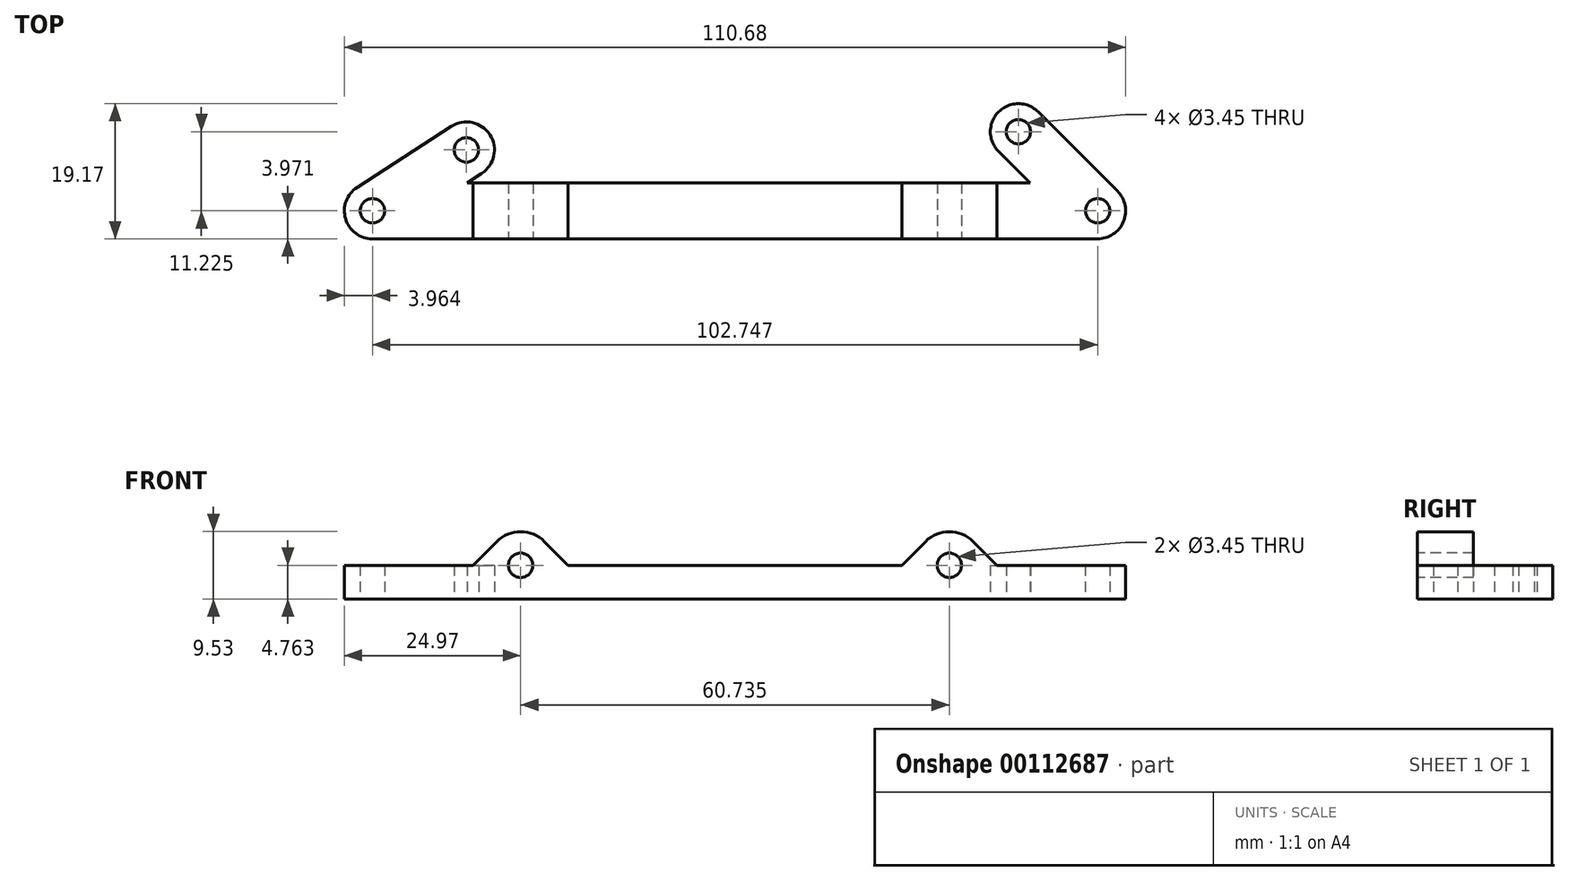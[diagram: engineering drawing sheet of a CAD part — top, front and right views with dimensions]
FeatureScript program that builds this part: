
annotation { "Feature Type Name" : "Feature", "Feature Type Description" : "" }
export const myFeature = defineFeature(function(context is Context, id is Id, definition is map)
    precondition{}
    {
        {
            var Q0;
            Q0=qCreatedBy(makeId("Top.planeOp"),FACE);
            var sketch = newSketch(context, id + "F0", { "sketchPlane" : qUnion([Q0])});
            skLineSegment(sketch, "E0", {"start": v(0, 0) * mm, "end": v(-79.74, 0) * mm});
            skLineSegment(sketch, "E1", {"start": v(0, 0) * mm, "end": v(-4.45, 4.45) * mm});
            skLineSegment(sketch, "E2", {"start": v(-79.74, 0) * mm, "end": v(-77.68, 1.33) * mm});
            skLineSegment(sketch, "E3", {"start": v(-39.87, 0) * mm, "end": v(-39.87, -7.94) * mm, "construction": true});
            skLineSegment(sketch, "E4", {"start": v(-93.17, -7.94) * mm, "end": v(9.58, -7.94) * mm});
            skLineSegment(sketch, "E5", {"start": v(-77.68, 1.33) * mm, "end": v(-82, 8) * mm, "construction": true});
            skLineSegment(sketch, "E6", {"start": v(-4.45, 4.45) * mm, "end": v(1.16, 10.06) * mm, "construction": true});
            skArc(sketch, "E7", {"start": v(-95.32, -0.64) * mm, "mid": v(-96.97, -5.1) * mm, "end": v(-93.17, -7.94) * mm});
            skArc(sketch, "E8", {"start": v(9.58, -7.94) * mm, "mid": v(13.25, -5.49) * mm, "end": v(12.39, -1.16) * mm});
            skArc(sketch, "E9", {"start": v(-77.68, 1.33) * mm, "mid": v(-76.51, 6.82) * mm, "end": v(-82, 8) * mm});
            skArc(sketch, "E10", {"start": v(1.16, 10.06) * mm, "mid": v(-4.45, 10.06) * mm, "end": v(-4.45, 4.45) * mm});
            skLineSegment(sketch, "E11", {"start": v(-93.17, -3.97) * mm, "end": v(-79.84, 4.66) * mm, "construction": true});
            skLineSegment(sketch, "E12", {"start": v(-95.32, -0.64) * mm, "end": v(-82, 8) * mm});
            skLineSegment(sketch, "E13", {"start": v(1.16, 10.06) * mm, "end": v(12.39, -1.16) * mm});
            skLineSegment(sketch, "E14", {"start": v(-1.64, 7.26) * mm, "end": v(9.58, -3.97) * mm, "construction": true});
            skCircle(sketch, "E15", {"center": v(-79.84, 4.66) * mm, "radius": 1.73 * mm});
            skCircle(sketch, "E16", {"center": v(-93.17, -3.97) * mm, "radius": 1.73 * mm});
            skCircle(sketch, "E17", {"center": v(-1.64, 7.26) * mm, "radius": 1.73 * mm});
            skCircle(sketch, "E18", {"center": v(9.58, -3.97) * mm, "radius": 1.73 * mm});
            skLineSegment(sketch, "E19", {"start": v(-39.87, 0) * mm, "end": v(-39.87, 2.49) * mm, "construction": true});
            skSolve(sketch);
        }
        {
            var Q0;
            Q0=qSketchRegion(id+"F0",true);
            extrude(context, id + "F1", {"entities" : qUnion([Q0]), "depth" : 4.76 * mm});
        }
        {
            var Q0;
            Q0=makeQuery(id+"F1.opExtrude","SWEPT_FACE",FACE,{"disambiguationData":[OSD([sQuery(id+"F0.wireOp",EDGE,"E4")])]});
            var sketch = newSketch(context, id + "F2", { "sketchPlane" : qUnion([Q0])});
            skLineSegment(sketch, "E20", {"start": v(-93.17, 2.38) * mm, "end": v(-72.16, 2.38) * mm});
            skLineSegment(sketch, "E21", {"start": v(-72.16, 2.38) * mm, "end": v(-72.16, 4.76) * mm});
            skLineSegment(sketch, "E22", {"start": v(-72.16, 2.38) * mm, "end": v(-11.42, 2.38) * mm});
            skLineSegment(sketch, "E23", {"start": v(-11.42, 2.38) * mm, "end": v(9.58, 2.38) * mm});
            skLineSegment(sketch, "E24", {"start": v(-11.42, 2.38) * mm, "end": v(-11.42, 4.76) * mm});
            skArc(sketch, "E25", {"start": v(-8.06, 8.13) * mm, "mid": v(-11.42, 9.53) * mm, "end": v(-14.8, 8.13) * mm});
            skLineSegment(sketch, "E26", {"start": v(-14.8, 8.13) * mm, "end": v(-18.16, 4.76) * mm});
            skLineSegment(sketch, "E27", {"start": v(-8.06, 8.13) * mm, "end": v(-4.69, 4.76) * mm});
            skLineSegment(sketch, "E28", {"start": v(-18.16, 4.76) * mm, "end": v(-4.69, 4.76) * mm});
            skLineSegment(sketch, "E29", {"start": v(-78.9, 4.76) * mm, "end": v(-65.42, 4.76) * mm});
            skLineSegment(sketch, "E30", {"start": v(-78.9, 4.76) * mm, "end": v(-75.53, 8.13) * mm});
            skLineSegment(sketch, "E31", {"start": v(-65.42, 4.76) * mm, "end": v(-68.8, 8.13) * mm});
            skArc(sketch, "E32", {"start": v(-68.8, 8.13) * mm, "mid": v(-72.16, 9.52) * mm, "end": v(-75.53, 8.13) * mm});
            skSolve(sketch);
        }
        {
            var Q0;
            Q0=qSketchRegion(id+"F2",true);
            var Q1;
            Q1=makeQuery(id+"F1.opExtrude","SWEPT_FACE",FACE,{"disambiguationData":[OSD([sQuery(id+"F0.wireOp",EDGE,"E0")])]});
            extrude(context, id + "F3", {"entities" : qUnion([Q0]), "operationType" : NewBodyOperationType.ADD, "endBound" : BoundingType.UP_TO_SURFACE, "oppositeDirection" : true, "endBoundEntityFace" : qUnion([Q1]), "depth" : 25.4 * mm});
        }
        {
            var Q0;
            Q0=makeQuery(id+"F3.boolean.opBoolean","MERGE",FACE,{"derivedFrom":[makeQuery(id+"F1.opExtrude","SWEPT_FACE",FACE,{"disambiguationData":[OSD([sQuery(id+"F0.wireOp",EDGE,"E4")])]}),makeQuery(id+"F3.opExtrude","CAP_FACE",FACE,{"disambiguationData":[OSD([sQuery(id+"F2.wireOp",EDGE,"E25"),sQuery(id+"F2.wireOp",EDGE,"E26"),sQuery(id+"F2.wireOp",EDGE,"E27"),sQuery(id+"F2.wireOp",EDGE,"E28")])],"isStart":true}),makeQuery(id+"F3.opExtrude","CAP_FACE",FACE,{"disambiguationData":[OSD([sQuery(id+"F2.wireOp",EDGE,"E29"),sQuery(id+"F2.wireOp",EDGE,"E30"),sQuery(id+"F2.wireOp",EDGE,"E31"),sQuery(id+"F2.wireOp",EDGE,"E32")])],"isStart":true})]});
            var sketch = newSketch(context, id + "F4", { "sketchPlane" : qUnion([Q0])});
            skCircle(sketch, "E33", {"center": v(-72.16, 4.76) * mm, "radius": 1.73 * mm});
            skCircle(sketch, "E34", {"center": v(-11.42, 4.76) * mm, "radius": 1.73 * mm});
            skSolve(sketch);
        }
        {
            var Q0;
            Q0=qSketchRegion(id+"F4",true);
            var Q1;
            {var subQ0=sQuery(id+"F0.wireOp",EDGE,"E0");Q1=makeQuery(id+"F3.boolean.opBoolean","MERGE",FACE,{"derivedFrom":[makeQuery(id+"F1.opExtrude","SWEPT_FACE",FACE,{"disambiguationData":[OSD([subQ0])]}),makeQuery(id+"F3.opExtrude","CAP_FACE",FACE,{"disambiguationData":[OSD([subQ0]),ownerDisambiguation([makeQuery(id+"F3.opExtrude","SWEPT_BODY",BODY,{"disambiguationData":[OSD([sQuery(id+"F2.wireOp",EDGE,"E25"),sQuery(id+"F2.wireOp",EDGE,"E26"),sQuery(id+"F2.wireOp",EDGE,"E27"),sQuery(id+"F2.wireOp",EDGE,"E28")])]})])],"isStart":false}),makeQuery(id+"F3.opExtrude","CAP_FACE",FACE,{"disambiguationData":[OSD([subQ0]),ownerDisambiguation([makeQuery(id+"F3.opExtrude","SWEPT_BODY",BODY,{"disambiguationData":[OSD([sQuery(id+"F2.wireOp",EDGE,"E29"),sQuery(id+"F2.wireOp",EDGE,"E30"),sQuery(id+"F2.wireOp",EDGE,"E31"),sQuery(id+"F2.wireOp",EDGE,"E32")])]})])],"isStart":false})]});}
            extrude(context, id + "F5", {"entities" : qUnion([Q0]), "operationType" : NewBodyOperationType.REMOVE, "endBound" : BoundingType.UP_TO_SURFACE, "oppositeDirection" : true, "endBoundEntityFace" : qUnion([Q1]), "depth" : 25.4 * mm});
        }
    });
